FCSTD DOCUMENT
Label: PR_007
objects: Sketcher::SketchObject×1
note: 1 computed .brp shape members not serialized (recipe doc carries the construction recipe); baked Part::Feature solids carry a one-line shape summary decoded from their .brp

FEATURE [Sketcher::SketchObject] Sketch
  sketch-geometry (8):
    g0: LineSegment StartX=14.1421 StartY=-954.92 StartZ=0 EndX=235.858 EndY=-954.92 EndZ=0
    g1: LineSegment StartX=14.1421 StartY=-954.92 StartZ=0 EndX=0 EndY=-969.062 EndZ=0
    g2: LineSegment StartX=0 StartY=-969.062 StartZ=0 EndX=0 EndY=-1004.92 EndZ=0
    g3: LineSegment StartX=235.858 StartY=-954.92 StartZ=0 EndX=250 EndY=-969.062 EndZ=0
    g4: LineSegment StartX=250 StartY=-969.062 StartZ=0 EndX=250 EndY=-1004.92 EndZ=0
    g5: LineSegment StartX=50 StartY=-1054.92 StartZ=0 EndX=200 EndY=-1054.92 EndZ=0
    g6: ArcOfCircle CenterX=50 CenterY=-1004.92 CenterZ=0 NormalX=0 NormalY=0 NormalZ=1 Radius=50 StartAngle=3.14159 EndAngle=4.71239
    g7: ArcOfCircle CenterX=200 CenterY=-1004.92 CenterZ=0 NormalX=0 NormalY=0 NormalZ=1 Radius=50 StartAngle=4.71239 EndAngle=6.28319
  constraints (22):
    c: Horizontal(g0)
    c: DistanceY(g0) = -954.92
    c: Coincident(g1,g0)
    c: Coincident(g2,g1)
    c: Vertical(g2)
    c: Coincident(g3,g0)
    c: Coincident(g4,g3)
    c: Vertical(g4)
    c: Horizontal(g5)
    c: Tangent(g6,g2)
    c: Tangent(g5,g6)
    c: Tangent(g7,g4)
    c: Tangent(g7,g5)
    c: DistanceY(g0,g5) = -100
    c: DistanceX(g2,g4) = 250
    c: DistanceX(g2) = 0
    c: Radius(g6) = 50
    c: Radius(g7) = 50
    c: Distance(g1) = 20
    c: Distance(g3) = 20
    c: Angle(g2,g1) = 2.35619
    c: Angle(g3,g4) = 2.35619
